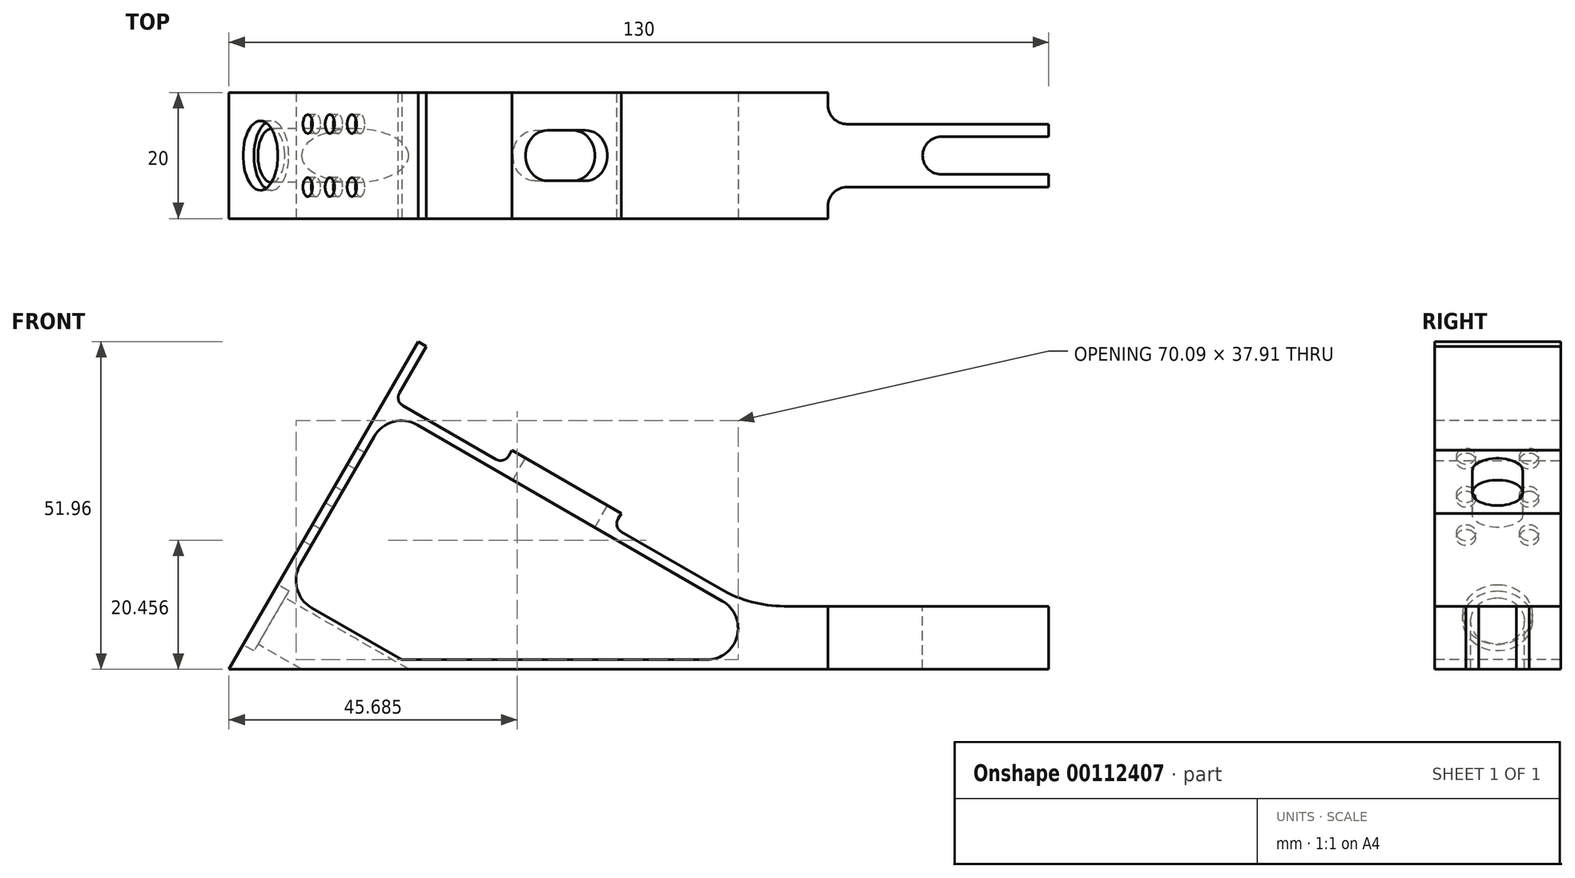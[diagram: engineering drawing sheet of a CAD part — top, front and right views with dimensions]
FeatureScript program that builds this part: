
annotation { "Feature Type Name" : "Feature", "Feature Type Description" : "" }
export const myFeature = defineFeature(function(context is Context, id is Id, definition is map)
    precondition{}
    {
        {
            var Q0;
            Q0=qCreatedBy(makeId("Front.planeOp"),FACE);
            var sketch = newSketch(context, id + "F0", { "sketchPlane" : qUnion([Q0])});
            skLineSegment(sketch, "E0", {"start": v(0, 0) * mm, "end": v(130, 0) * mm});
            skLineSegment(sketch, "E1", {"start": v(130, 0) * mm, "end": v(130, 10) * mm});
            skLineSegment(sketch, "E2", {"start": v(130, 10) * mm, "end": v(88.04, 10) * mm});
            skLineSegment(sketch, "E3", {"start": v(78.04, 12.68) * mm, "end": v(62.24, 21.8) * mm});
            skLineSegment(sketch, "E4", {"start": v(27.05, 43.85) * mm, "end": v(31.3, 51.21) * mm});
            skLineSegment(sketch, "E5", {"start": v(31.3, 51.21) * mm, "end": v(30, 51.96) * mm});
            skLineSegment(sketch, "E6", {"start": v(30, 51.96) * mm, "end": v(0, 0) * mm});
            skArc(sketch, "E7", {"start": v(78.04, 12.68) * mm, "mid": v(82.86, 10.68) * mm, "end": v(88.04, 10) * mm});
            skLineSegment(sketch, "E8", {"start": v(29.88, 38.75) * mm, "end": v(78.24, 10.83) * mm});
            skLineSegment(sketch, "E9", {"start": v(23.05, 36.92) * mm, "end": v(11.3, 16.57) * mm});
            skLineSegment(sketch, "E10", {"start": v(27.4, 1.5) * mm, "end": v(75.74, 1.5) * mm});
            skPoint(sketch, "E11.visualSharp", {"position": v(25.55, 41.25) * mm});
            skArc(sketch, "E11.filletArc", {"start": v(29.88, 38.75) * mm, "mid": v(26.09, 39.25) * mm, "end": v(23.05, 36.92) * mm});
            skPoint(sketch, "E12.visualSharp", {"position": v(94.4, 1.5) * mm});
            skArc(sketch, "E12.filletArc", {"start": v(75.74, 1.5) * mm, "mid": v(80.57, 5.2) * mm, "end": v(78.24, 10.83) * mm});
            skLineSegment(sketch, "E13", {"start": v(27.4, 1.5) * mm, "end": v(13.13, 9.74) * mm});
            skPoint(sketch, "E14.visualSharp", {"position": v(8.8, 12.24) * mm});
            skArc(sketch, "E14.filletArc", {"start": v(11.3, 16.57) * mm, "mid": v(10.8, 12.78) * mm, "end": v(13.13, 9.74) * mm});
            skLineSegment(sketch, "E15", {"start": v(44.37, 33.85) * mm, "end": v(44.87, 34.72) * mm});
            skLineSegment(sketch, "E16", {"start": v(44.87, 34.72) * mm, "end": v(62.2, 24.72) * mm});
            skLineSegment(sketch, "E17", {"start": v(62.2, 24.72) * mm, "end": v(61.7, 23.85) * mm});
            skLineSegment(sketch, "E18.trimOffspring", {"start": v(42.32, 33.3) * mm, "end": v(27.6, 41.8) * mm});
            skPoint(sketch, "E19.visualSharp", {"position": v(43.62, 32.55) * mm});
            skArc(sketch, "E19.filletArc", {"start": v(42.32, 33.3) * mm, "mid": v(43.46, 33.15) * mm, "end": v(44.37, 33.85) * mm});
            skPoint(sketch, "E20.visualSharp", {"position": v(60.94, 22.55) * mm});
            skArc(sketch, "E20.filletArc", {"start": v(61.7, 23.85) * mm, "mid": v(61.54, 22.71) * mm, "end": v(62.24, 21.8) * mm});
            skPoint(sketch, "E21.visualSharp", {"position": v(26.3, 42.55) * mm});
            skArc(sketch, "E21.filletArc", {"start": v(27.05, 43.85) * mm, "mid": v(26.9, 42.71) * mm, "end": v(27.6, 41.8) * mm});
            skSolve(sketch);
        }
        {
            var Q0;
            Q0=makeQuery(id+"F0.imprint","IMPRINT",FACE,{"disambiguationData":[TD([[makeQuery(id+"F0.imprint","IMPRINT",EDGE,{"derivedFrom":sQuery(id+"F0.wireOp",EDGE,"E0")}),1.0]])]});
            var Q1;
            Q1=makeQuery(id+"F0.imprint","IMPRINT",FACE,{"disambiguationData":[TD([[makeQuery(id+"F0.imprint","IMPRINT",EDGE,{"derivedFrom":sQuery(id+"F0.wireOp",EDGE,"E8")}),-1.0]])]});
            extrude(context, id + "F1", {"entities" : qUnion([Q0, Q1]), "endBound" : BoundingType.SYMMETRIC, "depth" : 20 * mm});
        }
        {
            var Q0;
            Q0=makeQuery(id+"F1.opExtrude","CAP_FACE",FACE,{"disambiguationData":[OSD([sQuery(id+"F0.wireOp",EDGE,"E0"),sQuery(id+"F0.wireOp",EDGE,"E1"),sQuery(id+"F0.wireOp",EDGE,"E2"),sQuery(id+"F0.wireOp",EDGE,"E3"),sQuery(id+"F0.wireOp",EDGE,"E4"),sQuery(id+"F0.wireOp",EDGE,"E5"),sQuery(id+"F0.wireOp",EDGE,"E6"),sQuery(id+"F0.wireOp",EDGE,"E7"),sQuery(id+"F0.wireOp",EDGE,"E15"),sQuery(id+"F0.wireOp",EDGE,"E16"),sQuery(id+"F0.wireOp",EDGE,"E17"),sQuery(id+"F0.wireOp",EDGE,"E18.trimOffspring"),sQuery(id+"F0.wireOp",EDGE,"E19.filletArc"),sQuery(id+"F0.wireOp",EDGE,"E20.filletArc"),sQuery(id+"F0.wireOp",EDGE,"E21.filletArc")])],"isStart":false});
            var sketch = newSketch(context, id + "F2", { "sketchPlane" : qUnion([Q0])});
            skLineSegment(sketch, "E22.0", {"start": v(23.05, 36.92) * mm, "end": v(11.3, 16.57) * mm});
            skArc(sketch, "E22.1", {"start": v(29.88, 38.75) * mm, "mid": v(26.09, 39.25) * mm, "end": v(23.05, 36.92) * mm});
            skLineSegment(sketch, "E22.2", {"start": v(29.88, 38.75) * mm, "end": v(78.24, 10.83) * mm});
            skArc(sketch, "E22.3", {"start": v(11.3, 16.57) * mm, "mid": v(10.8, 12.78) * mm, "end": v(13.13, 9.74) * mm});
            skLineSegment(sketch, "E22.4", {"start": v(27.4, 1.5) * mm, "end": v(13.13, 9.74) * mm});
            skLineSegment(sketch, "E22.5", {"start": v(27.4, 1.5) * mm, "end": v(75.74, 1.5) * mm});
            skArc(sketch, "E22.6", {"start": v(75.74, 1.5) * mm, "mid": v(80.57, 5.2) * mm, "end": v(78.24, 10.83) * mm});
            skSolve(sketch);
        }
        {
            var Q0;
            Q0=makeQuery(id+"F2.imprint","IMPRINT",FACE,{"disambiguationData":[TD([[makeQuery(id+"F2.imprint","IMPRINT",EDGE,{"derivedFrom":sQuery(id+"F2.wireOp",EDGE,"E22.0")}),1.0]])]});
            extrude(context, id + "F3", {"entities" : qUnion([Q0]), "operationType" : NewBodyOperationType.REMOVE, "endBound" : BoundingType.THROUGH_ALL, "oppositeDirection" : true, "depth" : 25 * mm, "hasSecondDirection" : true, "secondDirectionBound" : SecondDirectionBoundingType.THROUGH_ALL, "secondDirectionOppositeDirection" : false, "secondDirectionDepth" : 25 * mm});
        }
        {
            var Q0;
            Q0=makeQuery(id+"F1.opExtrude","SWEPT_FACE",FACE,{"disambiguationData":[OSD([sQuery(id+"F0.wireOp",EDGE,"E6")])]});
            var sketch = newSketch(context, id + "F4", { "sketchPlane" : qUnion([Q0])});
            skLineSegment(sketch, "E23", {"start": v(-10.87, 10) * mm, "end": v(10.87, 10) * mm, "construction": true});
            skLineSegment(sketch, "E24", {"start": v(0, 0) * mm, "end": v(0, 16.5) * mm, "construction": true});
            skPoint(sketch, "E24.endSnap0", {"position": v(0, 10) * mm});
            skCircle(sketch, "E25", {"center": v(0, 10) * mm, "radius": 5.5 * mm});
            skLineSegment(sketch, "E26", {"start": v(-5, 20.56) * mm, "end": v(-5, 57.44) * mm, "construction": true});
            skLineSegment(sketch, "E27", {"start": v(-8.05, 25) * mm, "end": v(5.61, 25) * mm, "construction": true});
            skLineSegment(sketch, "E28", {"start": v(5, 20.9) * mm, "end": v(5, 57.65) * mm, "construction": true});
            skLineSegment(sketch, "E29", {"start": v(-7.73, 32) * mm, "end": v(5.77, 32) * mm, "construction": true});
            skLineSegment(sketch, "E30", {"start": v(-7.4, 39) * mm, "end": v(6.91, 39) * mm, "construction": true});
            skCircle(sketch, "E31", {"center": v(-5, 25) * mm, "radius": 1.5 * mm});
            skCircle(sketch, "E32", {"center": v(-5, 32) * mm, "radius": 1.5 * mm});
            skCircle(sketch, "E33", {"center": v(-5, 39) * mm, "radius": 1.5 * mm});
            skCircle(sketch, "E34", {"center": v(5, 39) * mm, "radius": 1.5 * mm});
            skCircle(sketch, "E35", {"center": v(5, 32) * mm, "radius": 1.5 * mm});
            skCircle(sketch, "E36", {"center": v(5, 25) * mm, "radius": 1.5 * mm});
            skCircle(sketch, "E37", {"center": v(0, 10) * mm, "radius": 4.25 * mm});
            skSolve(sketch);
        }
        {
            var Q0;
            Q0=makeQuery(id+"F4.imprint","IMPRINT",FACE,{"disambiguationData":[TD([[makeQuery(id+"F4.imprint","IMPRINT",EDGE,{"derivedFrom":sQuery(id+"F4.wireOp",EDGE,"E31")}),1.0]])]});
            var Q1;
            Q1=makeQuery(id+"F4.imprint","IMPRINT",FACE,{"disambiguationData":[TD([[makeQuery(id+"F4.imprint","IMPRINT",EDGE,{"derivedFrom":sQuery(id+"F4.wireOp",EDGE,"E32")}),1.0]])]});
            var Q2;
            Q2=makeQuery(id+"F4.imprint","IMPRINT",FACE,{"disambiguationData":[TD([[makeQuery(id+"F4.imprint","IMPRINT",EDGE,{"derivedFrom":sQuery(id+"F4.wireOp",EDGE,"E33")}),1.0]])]});
            var Q3;
            Q3=makeQuery(id+"F4.imprint","IMPRINT",FACE,{"disambiguationData":[TD([[makeQuery(id+"F4.imprint","IMPRINT",EDGE,{"derivedFrom":sQuery(id+"F4.wireOp",EDGE,"E34")}),1.0]])]});
            var Q4;
            Q4=makeQuery(id+"F4.imprint","IMPRINT",FACE,{"disambiguationData":[TD([[makeQuery(id+"F4.imprint","IMPRINT",EDGE,{"derivedFrom":sQuery(id+"F4.wireOp",EDGE,"E35")}),1.0]])]});
            var Q5;
            Q5=makeQuery(id+"F4.imprint","IMPRINT",FACE,{"disambiguationData":[TD([[makeQuery(id+"F4.imprint","IMPRINT",EDGE,{"derivedFrom":sQuery(id+"F4.wireOp",EDGE,"E36")}),1.0]])]});
            var Q6;
            Q6=makeQuery(id+"F3.boolean.opBoolean","COPY",FACE,{"derivedFrom":makeQuery(id+"F3.opExtrude","SWEPT_FACE",FACE,{"disambiguationData":[OSD([sQuery(id+"F2.wireOp",EDGE,"E22.0")])]})});
            extrude(context, id + "F5", {"entities" : qUnion([Q0, Q1, Q2, Q3, Q4, Q5]), "operationType" : NewBodyOperationType.REMOVE, "endBound" : BoundingType.UP_TO_SURFACE, "oppositeDirection" : true, "endBoundEntityFace" : qUnion([Q6]), "depth" : 25 * mm});
        }
        {
            var Q0;
            Q0=makeQuery(id+"F4.imprint","IMPRINT",FACE,{"disambiguationData":[TD([[makeQuery(id+"F4.imprint","IMPRINT",EDGE,{"derivedFrom":sQuery(id+"F4.wireOp",EDGE,"E37")}),1.0]])]});
            extrude(context, id + "F6", {"entities" : qUnion([Q0]), "operationType" : NewBodyOperationType.REMOVE, "endBound" : BoundingType.THROUGH_ALL, "oppositeDirection" : true, "depth" : 25 * mm});
        }
        {
            var Q0;
            Q0=makeQuery(id+"F4.imprint","IMPRINT",FACE,{"disambiguationData":[TD([[makeQuery(id+"F4.imprint","IMPRINT",EDGE,{"derivedFrom":sQuery(id+"F4.wireOp",EDGE,"E25")}),1.0]])]});
            extrude(context, id + "F7", {"entities" : qUnion([Q0]), "operationType" : NewBodyOperationType.REMOVE, "oppositeDirection" : true, "depth" : 2 * mm});
        }
        {
            var Q0;
            Q0=makeQuery(id+"F1.opExtrude","SWEPT_FACE",FACE,{"disambiguationData":[OSD([sQuery(id+"F0.wireOp",EDGE,"E2")])]});
            var sketch = newSketch(context, id + "F8", { "sketchPlane" : qUnion([Q0])});
            skLineSegment(sketch, "E38.bottom", {"start": v(130, -5) * mm, "end": v(98, -5) * mm});
            skLineSegment(sketch, "E38.top", {"start": v(130, 5) * mm, "end": v(98, 5) * mm});
            skLineSegment(sketch, "E38.left", {"start": v(130, -5) * mm, "end": v(130, 5) * mm});
            skLineSegment(sketch, "E38.right", {"start": v(95, -5) * mm, "end": v(95, 5) * mm});
            skLineSegment(sketch, "E39", {"start": v(95, 8) * mm, "end": v(95, 10) * mm});
            skLineSegment(sketch, "E40", {"start": v(95, -8) * mm, "end": v(95, -10) * mm});
            skPoint(sketch, "E41.visualSharp", {"position": v(95, -5) * mm});
            skArc(sketch, "E41.filletArc", {"start": v(98, -5) * mm, "mid": v(95.88, -5.88) * mm, "end": v(95, -8) * mm});
            skPoint(sketch, "E42.visualSharp", {"position": v(95, 5) * mm});
            skArc(sketch, "E42.filletArc", {"start": v(95, 8) * mm, "mid": v(95.88, 5.88) * mm, "end": v(98, 5) * mm});
            skLineSegment(sketch, "E43.bottom", {"start": v(130, -3) * mm, "end": v(113, -3) * mm});
            skLineSegment(sketch, "E43.top", {"start": v(130, 3) * mm, "end": v(113, 3) * mm});
            skLineSegment(sketch, "E43.left", {"start": v(130, -3) * mm, "end": v(130, 3) * mm});
            skLineSegment(sketch, "E43.right", {"start": v(113, -3) * mm, "end": v(113, 3) * mm});
            skArc(sketch, "E44", {"start": v(113, 3) * mm, "mid": v(110, 0) * mm, "end": v(113, -3) * mm});
            skSolve(sketch);
        }
        {
            var Q0;
            Q0 = qSketchRegion(id + "F8", true);
            var Q1;
            {var subQ4=sQuery(id+"F8.wireOp",EDGE,"E38.bottom");Q1=makeQuery(id+"F8.imprint","IMPRINT",FACE,{"disambiguationData":[TD([[makeQuery(id+"F8.imprint","IMPRINT",EDGE,{"derivedFrom":subQ4}),1.0]])]});}
            var Q2;
            {var subQ4=sQuery(id+"F8.wireOp",EDGE,"E38.top");Q2=makeQuery(id+"F8.imprint","IMPRINT",FACE,{"disambiguationData":[TD([[makeQuery(id+"F8.imprint","IMPRINT",EDGE,{"derivedFrom":subQ4}),-1.0]])]});}
            extrude(context, id + "F9", {"entities" : qUnion([Q0, Q1, Q2]), "operationType" : NewBodyOperationType.REMOVE, "endBound" : BoundingType.THROUGH_ALL, "oppositeDirection" : true, "depth" : 25 * mm});
        }
        {
            var Q0;
            Q0=makeQuery(id+"F1.opExtrude","SWEPT_FACE",FACE,{"disambiguationData":[OSD([sQuery(id+"F0.wireOp",EDGE,"E16")])]});
            var sketch = newSketch(context, id + "F10", { "sketchPlane" : qUnion([Q0])});
            skLineSegment(sketch, "E45.bottom", {"start": v(28, -4) * mm, "end": v(35, -4) * mm});
            skLineSegment(sketch, "E45.top", {"start": v(28, 4) * mm, "end": v(35, 4) * mm});
            skLineSegment(sketch, "E45.left", {"start": v(28, -4) * mm, "end": v(28, 4) * mm});
            skLineSegment(sketch, "E45.right", {"start": v(35, -4) * mm, "end": v(35, 4) * mm});
            skArc(sketch, "E46", {"start": v(28, 4) * mm, "mid": v(24, 0) * mm, "end": v(28, -4) * mm});
            skArc(sketch, "E47", {"start": v(35, -4) * mm, "mid": v(39, 0) * mm, "end": v(35, 4) * mm});
            skSolve(sketch);
        }
        {
            var Q0;
            Q0=makeQuery(id+"F10.imprint","IMPRINT",FACE,{"disambiguationData":[TD([[makeQuery(id+"F10.imprint","IMPRINT",EDGE,{"derivedFrom":sQuery(id+"F10.wireOp",EDGE,"E45.left")}),1.0]])]});
            var Q1;
            Q1=makeQuery(id+"F10.imprint","IMPRINT",FACE,{"disambiguationData":[TD([[makeQuery(id+"F10.imprint","IMPRINT",EDGE,{"derivedFrom":sQuery(id+"F10.wireOp",EDGE,"E45.bottom")}),1.0]])]});
            var Q2;
            Q2=makeQuery(id+"F10.imprint","IMPRINT",FACE,{"disambiguationData":[TD([[makeQuery(id+"F10.imprint","IMPRINT",EDGE,{"derivedFrom":sQuery(id+"F10.wireOp",EDGE,"E45.right")}),-1.0]])]});
            var Q3;
            Q3=makeQuery(id+"F3.boolean.opBoolean","COPY",FACE,{"derivedFrom":makeQuery(id+"F3.opExtrude","SWEPT_FACE",FACE,{"disambiguationData":[OSD([sQuery(id+"F2.wireOp",EDGE,"E22.2")])]})});
            extrude(context, id + "F11", {"entities" : qUnion([Q0, Q1, Q2]), "operationType" : NewBodyOperationType.REMOVE, "endBound" : BoundingType.UP_TO_SURFACE, "oppositeDirection" : true, "endBoundEntityFace" : qUnion([Q3]), "depth" : 25 * mm});
        }
    });
